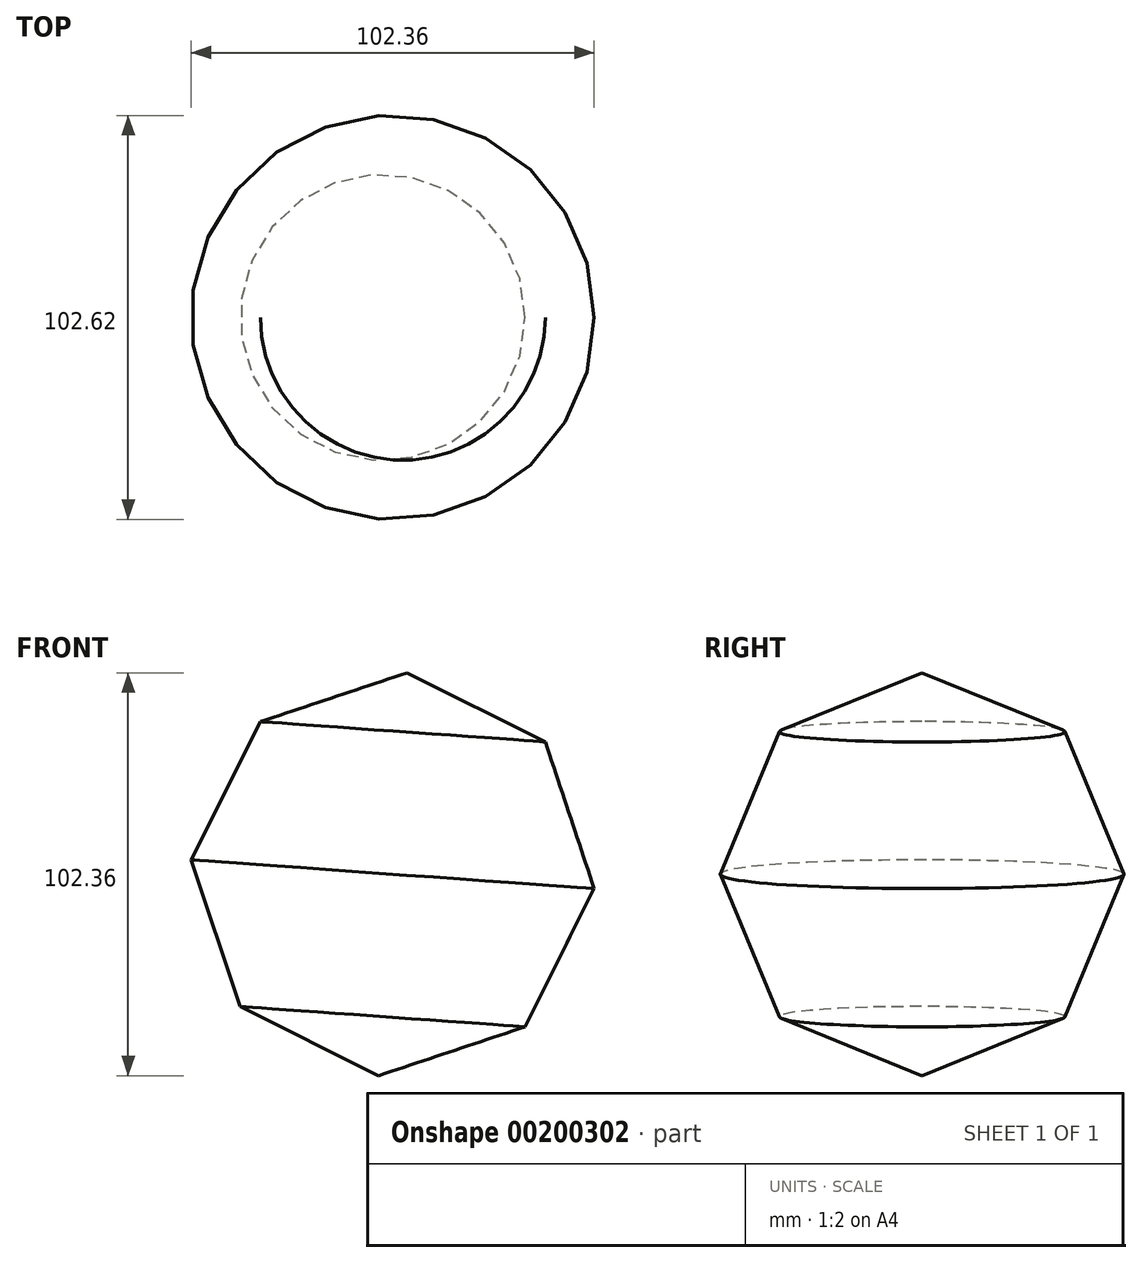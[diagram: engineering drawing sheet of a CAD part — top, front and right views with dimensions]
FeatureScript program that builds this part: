
annotation { "Feature Type Name" : "Feature", "Feature Type Description" : "" }
export const myFeature = defineFeature(function(context is Context, id is Id, definition is map)
    precondition{}
    {
        {
            var Q0;
            Q0=qCreatedBy(makeId("Front.planeOp"),FACE);
            var sketch = newSketch(context, id + "F0", { "sketchPlane" : qUnion([Q0])});
            skLineSegment(sketch, "E0.1", {"start": v(-3.64, -51.18) * mm, "end": v(-38.76, -33.61) * mm});
            skLineSegment(sketch, "E0.2", {"start": v(-38.76, -33.61) * mm, "end": v(-51.18, 3.64) * mm});
            skLineSegment(sketch, "E0.3", {"start": v(-51.18, 3.64) * mm, "end": v(-33.61, 38.76) * mm});
            skLineSegment(sketch, "E0.4", {"start": v(-33.61, 38.76) * mm, "end": v(3.64, 51.18) * mm});
            skPoint(sketch, "E0.0.midPoint", {"position": v(14.99, -44.97) * mm});
            skLineSegment(sketch, "E1", {"start": v(3.64, 51.18) * mm, "end": v(-3.64, -51.18) * mm});
            skSolve(sketch);
        }
        {
            var Q0;
            Q0=makeQuery(id+"F0.imprint","IMPRINT",FACE,{"disambiguationData":[TD([[makeQuery(id+"F0.imprint","IMPRINT",EDGE,{"derivedFrom":sQuery(id+"F0.wireOp",EDGE,"E0.1")}),-1.0]])]});
            var Q1;
            Q1=sQuery(id+"F0.wireOp",EDGE,"E1");
            revolve(context, id + "F1", {"entities" : qUnion([Q0]), "axis" : qUnion([Q1]), "revolveType" : RevolveType.FULL});
        }
    });
